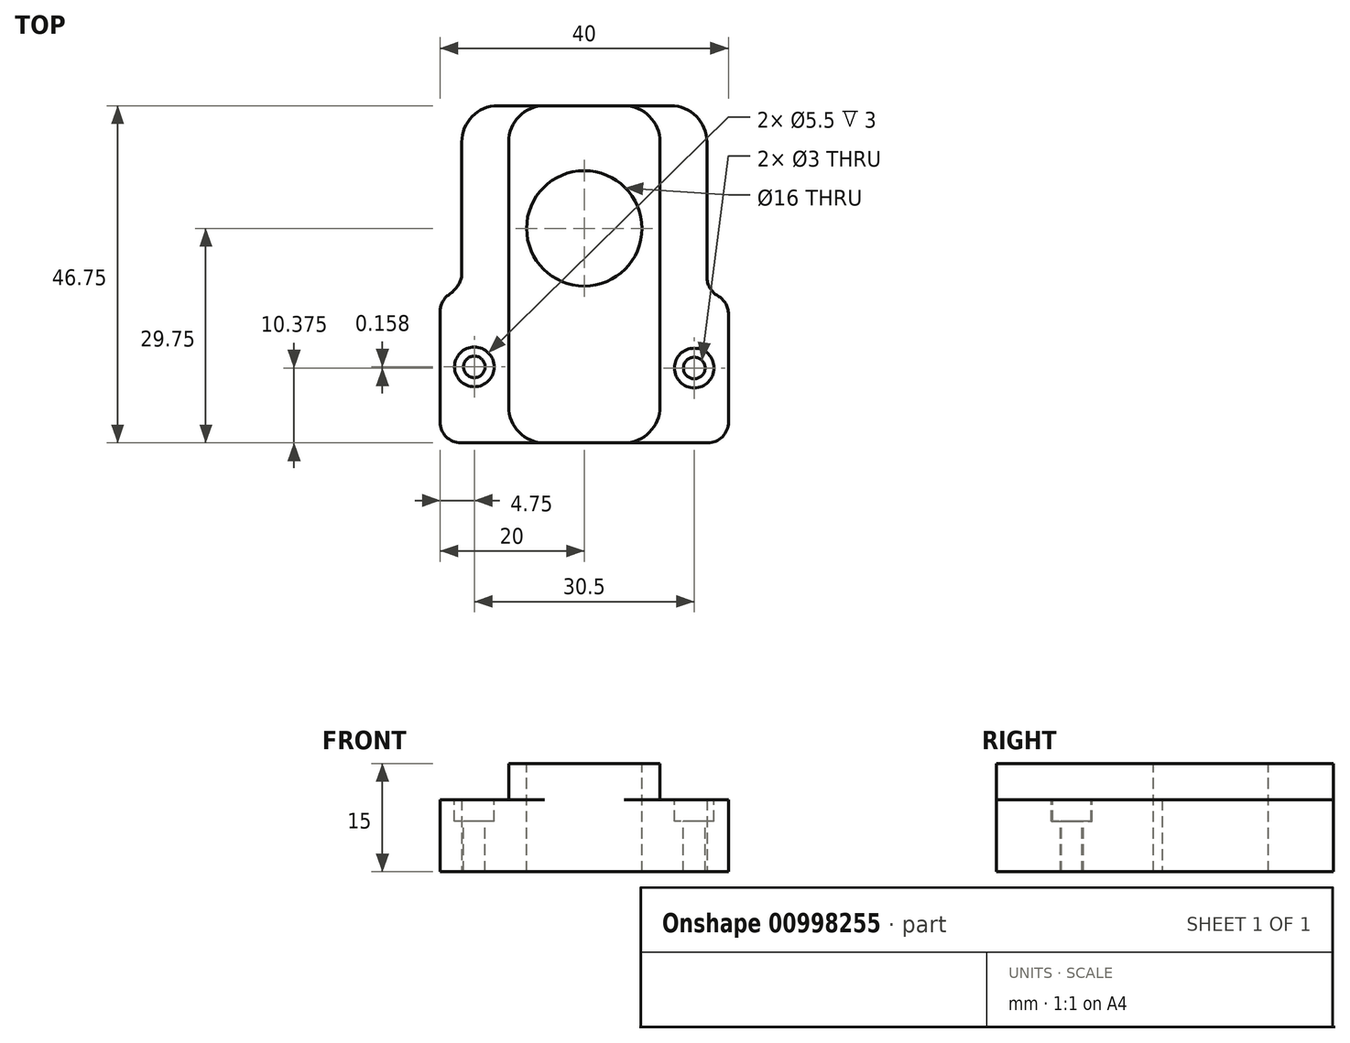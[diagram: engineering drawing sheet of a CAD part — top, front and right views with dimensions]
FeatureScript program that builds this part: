
annotation { "Feature Type Name" : "Feature", "Feature Type Description" : "" }
export const myFeature = defineFeature(function(context is Context, id is Id, definition is map)
    precondition{}
    {
        {
            var Q0;
            Q0=qCreatedBy(makeId("Top.planeOp"),FACE);
            var sketch = newSketch(context, id + "F0", { "sketchPlane" : qUnion([Q0])});
            skPoint(sketch, "E0.middle", {"position": v(0, 0) * mm});
            skLineSegment(sketch, "E1.bottom", {"start": v(17.13, -29.75) * mm, "end": v(-17.13, -29.75) * mm});
            skLineSegment(sketch, "E1.left", {"start": v(20, -26.88) * mm, "end": v(20, -11.87) * mm});
            skLineSegment(sketch, "E1.right", {"start": v(-20, -26.88) * mm, "end": v(-20, -11.56) * mm});
            skArc(sketch, "E2", {"start": v(-18.73, -9.17) * mm, "mid": v(-17.65, -8.12) * mm, "end": v(-17, -6.75) * mm});
            skArc(sketch, "E3", {"start": v(17, -6.75) * mm, "mid": v(17.41, -8.27) * mm, "end": v(18.53, -9.37) * mm});
            skPoint(sketch, "E4.visualSharp", {"position": v(-20, -9.75) * mm});
            skArc(sketch, "E4.filletArc", {"start": v(-18.73, -9.17) * mm, "mid": v(-19.66, -10.2) * mm, "end": v(-20, -11.56) * mm});
            skPoint(sketch, "E5.visualSharp", {"position": v(20, -9.75) * mm});
            skArc(sketch, "E5.filletArc", {"start": v(20, -11.87) * mm, "mid": v(19.6, -10.42) * mm, "end": v(18.53, -9.37) * mm});
            skPoint(sketch, "E6.visualSharp", {"position": v(20, -29.75) * mm});
            skArc(sketch, "E6.filletArc", {"start": v(17.13, -29.75) * mm, "mid": v(19.16, -28.9) * mm, "end": v(20, -26.88) * mm});
            skPoint(sketch, "E7.visualSharp", {"position": v(-20, -29.75) * mm});
            skArc(sketch, "E7.filletArc", {"start": v(-20, -26.88) * mm, "mid": v(-19.16, -28.9) * mm, "end": v(-17.13, -29.75) * mm});
            skLineSegment(sketch, "E8", {"start": v(-17, 12) * mm, "end": v(-17, -6.75) * mm});
            skLineSegment(sketch, "E9", {"start": v(-12, 17) * mm, "end": v(12, 17) * mm});
            skPoint(sketch, "E10.visualSharp", {"position": v(-17, 17) * mm});
            skArc(sketch, "E10.filletArc", {"start": v(-12, 17) * mm, "mid": v(-15.54, 15.54) * mm, "end": v(-17, 12) * mm});
            skLineSegment(sketch, "E11", {"start": v(17, -6.75) * mm, "end": v(17, 12) * mm});
            skPoint(sketch, "E12.visualSharp", {"position": v(17, 17) * mm});
            skArc(sketch, "E12.filletArc", {"start": v(17, 12) * mm, "mid": v(15.54, 15.54) * mm, "end": v(12, 17) * mm});
            skSolve(sketch);
        }
        {
            var Q0;
            Q0=makeQuery(id+"F0.imprint","IMPRINT",FACE,{"disambiguationData":[TD([[makeQuery(id+"F0.imprint","IMPRINT",EDGE,{"derivedFrom":sQuery(id+"F0.wireOp",EDGE,"E1.bottom")}),-1.0]])]});
            extrude(context, id + "F1", {"entities" : qUnion([Q0]), "depth" : 10 * mm, "offsetDistance" : 25 * mm});
        }
        {
            var Q0;
            Q0=makeQuery(id+"F1.opExtrude","CAP_FACE",FACE,{"disambiguationData":[OSD([sQuery(id+"F0.wireOp",EDGE,"E1.bottom"),sQuery(id+"F0.wireOp",EDGE,"E1.left"),sQuery(id+"F0.wireOp",EDGE,"E1.right"),sQuery(id+"F0.wireOp",EDGE,"E2"),sQuery(id+"F0.wireOp",EDGE,"E3"),sQuery(id+"F0.wireOp",EDGE,"E4.filletArc"),sQuery(id+"F0.wireOp",EDGE,"E5.filletArc"),sQuery(id+"F0.wireOp",EDGE,"E6.filletArc"),sQuery(id+"F0.wireOp",EDGE,"E7.filletArc"),sQuery(id+"F0.wireOp",EDGE,"E8"),sQuery(id+"F0.wireOp",EDGE,"E9"),sQuery(id+"F0.wireOp",EDGE,"E10.filletArc"),sQuery(id+"F0.wireOp",EDGE,"E11"),sQuery(id+"F0.wireOp",EDGE,"E12.filletArc")])],"isStart":false});
            var sketch = newSketch(context, id + "F2", { "sketchPlane" : qUnion([Q0])});
            skPoint(sketch, "E13.middle", {"position": v(0, -1.38) * mm});
            skLineSegment(sketch, "E14", {"start": v(-10.5, -24.75) * mm, "end": v(-10.5, 12) * mm});
            skLineSegment(sketch, "E15", {"start": v(-5.5, 17) * mm, "end": v(5.5, 17) * mm});
            skLineSegment(sketch, "E16", {"start": v(10.5, 12) * mm, "end": v(10.5, -24.75) * mm});
            skLineSegment(sketch, "E17", {"start": v(5.5, -29.75) * mm, "end": v(-5.5, -29.75) * mm});
            skPoint(sketch, "E18.visualSharp", {"position": v(-10.5, 17) * mm});
            skArc(sketch, "E18.filletArc", {"start": v(-5.5, 17) * mm, "mid": v(-9.04, 15.54) * mm, "end": v(-10.5, 12) * mm});
            skPoint(sketch, "E19.visualSharp", {"position": v(10.5, 17) * mm});
            skArc(sketch, "E19.filletArc", {"start": v(10.5, 12) * mm, "mid": v(9.04, 15.54) * mm, "end": v(5.5, 17) * mm});
            skPoint(sketch, "E20.visualSharp", {"position": v(10.5, -29.75) * mm});
            skArc(sketch, "E20.filletArc", {"start": v(5.5, -29.75) * mm, "mid": v(9.04, -28.29) * mm, "end": v(10.5, -24.75) * mm});
            skPoint(sketch, "E21.visualSharp", {"position": v(-10.5, -29.75) * mm});
            skArc(sketch, "E21.filletArc", {"start": v(-10.5, -24.75) * mm, "mid": v(-9.04, -28.29) * mm, "end": v(-5.5, -29.75) * mm});
            skSolve(sketch);
        }
        {
            var Q0;
            Q0=makeQuery(id+"F2.imprint","IMPRINT",FACE,{"disambiguationData":[TD([[makeQuery(id+"F2.imprint","IMPRINT",EDGE,{"derivedFrom":sQuery(id+"F2.wireOp",EDGE,"E14")}),-1.0]])]});
            extrude(context, id + "F3", {"entities" : qUnion([Q0]), "operationType" : NewBodyOperationType.ADD, "depth" : 5 * mm, "offsetDistance" : 25 * mm});
        }
        {
            var Q0;
            Q0=makeQuery(id+"F3.opExtrude","CAP_FACE",FACE,{"disambiguationData":[OSD([sQuery(id+"F2.wireOp",EDGE,"E14"),sQuery(id+"F2.wireOp",EDGE,"E15"),sQuery(id+"F2.wireOp",EDGE,"E16"),sQuery(id+"F2.wireOp",EDGE,"E17"),sQuery(id+"F2.wireOp",EDGE,"E18.filletArc"),sQuery(id+"F2.wireOp",EDGE,"E19.filletArc"),sQuery(id+"F2.wireOp",EDGE,"E20.filletArc"),sQuery(id+"F2.wireOp",EDGE,"E21.filletArc")])],"isStart":false});
            var sketch = newSketch(context, id + "F4", { "sketchPlane" : qUnion([Q0])});
            skCircle(sketch, "E22", {"center": v(0, 0) * mm, "radius": 8 * mm});
            skSolve(sketch);
        }
        {
            var Q0;
            Q0=makeQuery(id+"F4.imprint","IMPRINT",FACE,{"disambiguationData":[TD([[makeQuery(id+"F4.imprint","IMPRINT",EDGE,{"derivedFrom":sQuery(id+"F4.wireOp",EDGE,"E22")}),1.0]])]});
            extrude(context, id + "F5", {"entities" : qUnion([Q0]), "operationType" : NewBodyOperationType.REMOVE, "oppositeDirection" : true, "depth" : 25 * mm, "offsetDistance" : 25 * mm});
        }
        {
            var Q0;
            {var subQ0=sQuery(id+"F0.wireOp",EDGE,"E10.filletArc");var subQ1=sQuery(id+"F0.wireOp",EDGE,"E1.right");var subQ2=sQuery(id+"F0.wireOp",EDGE,"E9");var subQ3=sQuery(id+"F0.wireOp",EDGE,"E7.filletArc");var subQ4=sQuery(id+"F0.wireOp",EDGE,"E8");var subQ5=sQuery(id+"F0.wireOp",EDGE,"E1.bottom");var subQ6=sQuery(id+"F0.wireOp",EDGE,"E2");var subQ7=sQuery(id+"F0.wireOp",EDGE,"E4.filletArc");Q0=makeQuery(id+"F3.boolean.opBoolean","SPLIT",FACE,{"disambiguationData":[TD([makeQuery(id+"F1.opExtrude","SWEPT_FACE",FACE,{"disambiguationData":[OSD([subQ1])]})])],"derivedFrom":makeQuery(id+"F1.opExtrude","CAP_FACE",FACE,{"disambiguationData":[OSD([subQ5,sQuery(id+"F0.wireOp",EDGE,"E1.left"),subQ1,subQ6,sQuery(id+"F0.wireOp",EDGE,"E3"),subQ7,sQuery(id+"F0.wireOp",EDGE,"E5.filletArc"),sQuery(id+"F0.wireOp",EDGE,"E6.filletArc"),subQ3,subQ4,subQ2,subQ0,sQuery(id+"F0.wireOp",EDGE,"E11"),sQuery(id+"F0.wireOp",EDGE,"E12.filletArc")])],"isStart":false})});}
            var sketch = newSketch(context, id + "F6", { "sketchPlane" : qUnion([Q0])});
            skCircle(sketch, "E23", {"center": v(-15.25, -19.22) * mm, "radius": 1.5 * mm});
            skCircle(sketch, "E24", {"center": v(-15.25, -19.22) * mm, "radius": 2.75 * mm});
            skSolve(sketch);
        }
        {
            var Q0;
            Q0=makeQuery(id+"F6.imprint","IMPRINT",FACE,{"disambiguationData":[TD([[makeQuery(id+"F6.imprint","IMPRINT",EDGE,{"derivedFrom":sQuery(id+"F6.wireOp",EDGE,"E23")}),-1.0]])]});
            extrude(context, id + "F7", {"entities" : qUnion([Q0]), "operationType" : NewBodyOperationType.REMOVE, "oppositeDirection" : true, "depth" : 3 * mm, "offsetDistance" : 25 * mm});
        }
        {
            var Q0;
            {var subQ0=sQuery(id+"F0.wireOp",EDGE,"E10.filletArc");var subQ1=sQuery(id+"F0.wireOp",EDGE,"E1.right");var subQ2=sQuery(id+"F0.wireOp",EDGE,"E9");var subQ3=sQuery(id+"F0.wireOp",EDGE,"E7.filletArc");var subQ4=sQuery(id+"F0.wireOp",EDGE,"E8");var subQ5=sQuery(id+"F0.wireOp",EDGE,"E1.bottom");var subQ6=sQuery(id+"F0.wireOp",EDGE,"E2");var subQ7=sQuery(id+"F0.wireOp",EDGE,"E4.filletArc");Q0=makeQuery(id+"F7.boolean.opBoolean","SPLIT",FACE,{"disambiguationData":[TD([makeQuery(id+"F7.opExtrude","SWEPT_FACE",FACE,{"disambiguationData":[OSD([sQuery(id+"F6.wireOp",EDGE,"E23")])]})])],"derivedFrom":makeQuery(id+"F3.boolean.opBoolean","SPLIT",FACE,{"disambiguationData":[TD([makeQuery(id+"F1.opExtrude","SWEPT_FACE",FACE,{"disambiguationData":[OSD([subQ1])]})])],"derivedFrom":makeQuery(id+"F1.opExtrude","CAP_FACE",FACE,{"disambiguationData":[OSD([subQ5,sQuery(id+"F0.wireOp",EDGE,"E1.left"),subQ1,subQ6,sQuery(id+"F0.wireOp",EDGE,"E3"),subQ7,sQuery(id+"F0.wireOp",EDGE,"E5.filletArc"),sQuery(id+"F0.wireOp",EDGE,"E6.filletArc"),subQ3,subQ4,subQ2,subQ0,sQuery(id+"F0.wireOp",EDGE,"E11"),sQuery(id+"F0.wireOp",EDGE,"E12.filletArc")])],"isStart":false})})});}
            extrude(context, id + "F8", {"entities" : qUnion([Q0]), "operationType" : NewBodyOperationType.REMOVE, "oppositeDirection" : true, "depth" : 25 * mm, "offsetDistance" : 25 * mm});
        }
        {
            var Q0;
            {var subQ0=sQuery(id+"F0.wireOp",EDGE,"E5.filletArc");var subQ1=sQuery(id+"F0.wireOp",EDGE,"E12.filletArc");var subQ2=sQuery(id+"F0.wireOp",EDGE,"E9");var subQ3=sQuery(id+"F0.wireOp",EDGE,"E6.filletArc");var subQ4=sQuery(id+"F0.wireOp",EDGE,"E1.bottom");var subQ5=sQuery(id+"F0.wireOp",EDGE,"E11");var subQ6=sQuery(id+"F0.wireOp",EDGE,"E1.left");var subQ7=sQuery(id+"F0.wireOp",EDGE,"E3");Q0=makeQuery(id+"F3.boolean.opBoolean","SPLIT",FACE,{"disambiguationData":[TD([makeQuery(id+"F1.opExtrude","SWEPT_FACE",FACE,{"disambiguationData":[OSD([subQ6])]})])],"derivedFrom":makeQuery(id+"F1.opExtrude","CAP_FACE",FACE,{"disambiguationData":[OSD([subQ4,subQ6,sQuery(id+"F0.wireOp",EDGE,"E1.right"),sQuery(id+"F0.wireOp",EDGE,"E2"),subQ7,sQuery(id+"F0.wireOp",EDGE,"E4.filletArc"),subQ0,subQ3,sQuery(id+"F0.wireOp",EDGE,"E7.filletArc"),sQuery(id+"F0.wireOp",EDGE,"E8"),subQ2,sQuery(id+"F0.wireOp",EDGE,"E10.filletArc"),subQ5,subQ1])],"isStart":false})});}
            var sketch = newSketch(context, id + "F9", { "sketchPlane" : qUnion([Q0])});
            skCircle(sketch, "E25", {"center": v(15.25, -19.37) * mm, "radius": 2.75 * mm});
            skCircle(sketch, "E26", {"center": v(15.25, -19.37) * mm, "radius": 1.5 * mm});
            skSolve(sketch);
        }
        {
            var Q0;
            Q0=makeQuery(id+"F9.imprint","IMPRINT",FACE,{"disambiguationData":[TD([[makeQuery(id+"F9.imprint","IMPRINT",EDGE,{"derivedFrom":sQuery(id+"F9.wireOp",EDGE,"E25")}),1.0]])]});
            extrude(context, id + "F10", {"entities" : qUnion([Q0]), "operationType" : NewBodyOperationType.REMOVE, "oppositeDirection" : true, "depth" : 3 * mm, "offsetDistance" : 25 * mm});
        }
        {
            var Q0;
            {var subQ0=sQuery(id+"F0.wireOp",EDGE,"E5.filletArc");var subQ1=sQuery(id+"F0.wireOp",EDGE,"E12.filletArc");var subQ2=sQuery(id+"F0.wireOp",EDGE,"E9");var subQ3=sQuery(id+"F0.wireOp",EDGE,"E6.filletArc");var subQ4=sQuery(id+"F0.wireOp",EDGE,"E1.bottom");var subQ5=sQuery(id+"F0.wireOp",EDGE,"E11");var subQ6=sQuery(id+"F0.wireOp",EDGE,"E1.left");var subQ7=sQuery(id+"F0.wireOp",EDGE,"E3");Q0=makeQuery(id+"F10.boolean.opBoolean","SPLIT",FACE,{"disambiguationData":[TD([makeQuery(id+"F10.opExtrude","SWEPT_FACE",FACE,{"disambiguationData":[OSD([sQuery(id+"F9.wireOp",EDGE,"E26")])]})])],"derivedFrom":makeQuery(id+"F3.boolean.opBoolean","SPLIT",FACE,{"disambiguationData":[TD([makeQuery(id+"F1.opExtrude","SWEPT_FACE",FACE,{"disambiguationData":[OSD([subQ6])]})])],"derivedFrom":makeQuery(id+"F1.opExtrude","CAP_FACE",FACE,{"disambiguationData":[OSD([subQ4,subQ6,sQuery(id+"F0.wireOp",EDGE,"E1.right"),sQuery(id+"F0.wireOp",EDGE,"E2"),subQ7,sQuery(id+"F0.wireOp",EDGE,"E4.filletArc"),subQ0,subQ3,sQuery(id+"F0.wireOp",EDGE,"E7.filletArc"),sQuery(id+"F0.wireOp",EDGE,"E8"),subQ2,sQuery(id+"F0.wireOp",EDGE,"E10.filletArc"),subQ5,subQ1])],"isStart":false})})});}
            extrude(context, id + "F11", {"entities" : qUnion([Q0]), "operationType" : NewBodyOperationType.REMOVE, "oppositeDirection" : true, "depth" : 25 * mm, "offsetDistance" : 25 * mm});
        }
    });
